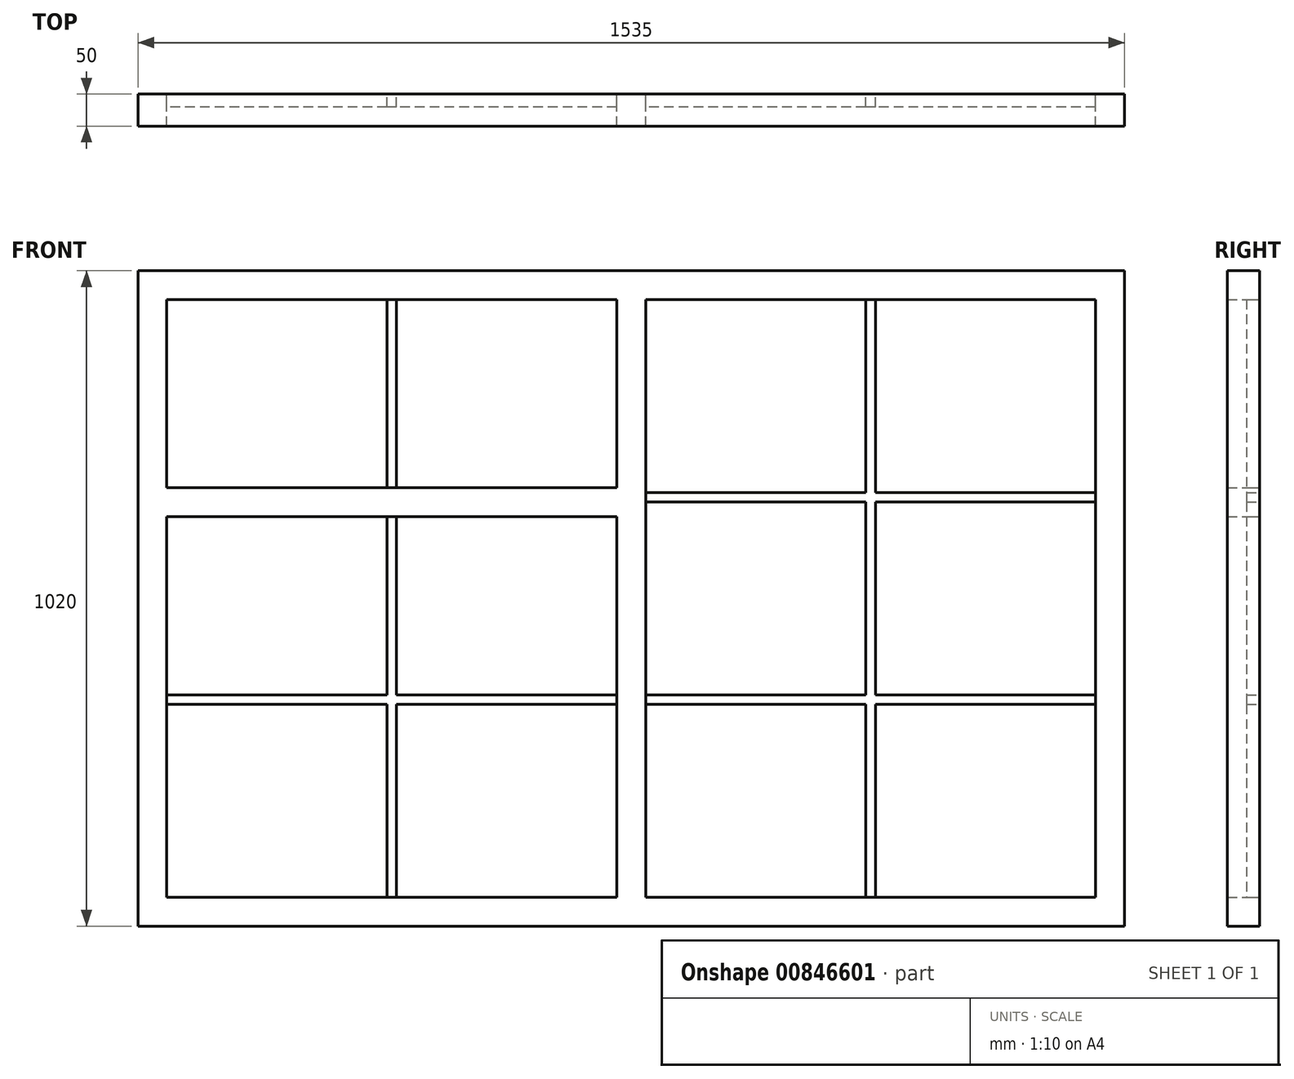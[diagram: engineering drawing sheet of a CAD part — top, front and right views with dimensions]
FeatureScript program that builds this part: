
annotation { "Feature Type Name" : "Feature", "Feature Type Description" : "" }
export const myFeature = defineFeature(function(context is Context, id is Id, definition is map)
    precondition{}
    {
        {
            var Q0;
            Q0=qCreatedBy(makeId("Front.planeOp"),FACE);
            var sketch = newSketch(context, id + "F0", { "sketchPlane" : qUnion([Q0])});
            skLineSegment(sketch, "E0.bottom", {"start": v(0, 0) * mm, "end": v(1535, 0) * mm});
            skLineSegment(sketch, "E0.top", {"start": v(0, 1020) * mm, "end": v(1535, 1020) * mm});
            skLineSegment(sketch, "E0.left", {"start": v(0, 0) * mm, "end": v(0, 1020) * mm});
            skLineSegment(sketch, "E0.right", {"start": v(1535, 0) * mm, "end": v(1535, 1020) * mm});
            skLineSegment(sketch, "E1.bottom", {"start": v(45, 975) * mm, "end": v(745, 975) * mm});
            skLineSegment(sketch, "E1.top", {"start": v(45, 45) * mm, "end": v(745, 45) * mm});
            skLineSegment(sketch, "E1.left", {"start": v(45, 975) * mm, "end": v(45, 45) * mm});
            skLineSegment(sketch, "E1.right", {"start": v(745, 975) * mm, "end": v(745, 45) * mm});
            skLineSegment(sketch, "E2.bottom", {"start": v(790, 975) * mm, "end": v(1490, 975) * mm});
            skLineSegment(sketch, "E2.top", {"start": v(790, 682.5) * mm, "end": v(1490, 682.5) * mm});
            skLineSegment(sketch, "E2.left", {"start": v(790, 975) * mm, "end": v(790, 682.5) * mm});
            skLineSegment(sketch, "E2.right", {"start": v(1490, 975) * mm, "end": v(1490, 682.5) * mm});
            skLineSegment(sketch, "E3.bottom", {"start": v(790, 637.5) * mm, "end": v(1490, 637.5) * mm});
            skLineSegment(sketch, "E3.top", {"start": v(790, 45) * mm, "end": v(1490, 45) * mm});
            skLineSegment(sketch, "E3.left", {"start": v(790, 637.5) * mm, "end": v(790, 45) * mm});
            skLineSegment(sketch, "E3.right", {"start": v(1490, 637.5) * mm, "end": v(1490, 45) * mm});
            skSolve(sketch);
        }
        {
            var Q0;
            Q0=qSketchRegion(id+"F0",true);
            extrude(context, id + "F1", {"entities" : qUnion([Q0]), "depth" : 50 * mm, "offsetDistance" : 25 * mm});
        }
        {
            var Q0;
            Q0=qCreatedBy(makeId("Front.planeOp"),FACE);
            var sketch = newSketch(context, id + "F2", { "sketchPlane" : qUnion([Q0])});
            skLineSegment(sketch, "E4.bottom", {"start": v(387.5, 975) * mm, "end": v(402.5, 975) * mm});
            skLineSegment(sketch, "E4.top", {"start": v(387.5, 45) * mm, "end": v(402.5, 45) * mm});
            skLineSegment(sketch, "E4.left", {"start": v(387.5, 975) * mm, "end": v(387.5, 675) * mm});
            skLineSegment(sketch, "E4.right", {"start": v(402.5, 975) * mm, "end": v(402.5, 675) * mm});
            skLineSegment(sketch, "E5.bottom", {"start": v(45, 675) * mm, "end": v(387.5, 675) * mm});
            skLineSegment(sketch, "E5.top", {"start": v(45, 660) * mm, "end": v(387.5, 660) * mm});
            skLineSegment(sketch, "E5.left", {"start": v(45, 675) * mm, "end": v(45, 660) * mm});
            skLineSegment(sketch, "E5.right", {"start": v(745, 675) * mm, "end": v(745, 660) * mm});
            skLineSegment(sketch, "E6.bottom", {"start": v(45, 360) * mm, "end": v(387.5, 360) * mm});
            skLineSegment(sketch, "E6.top", {"start": v(45, 345) * mm, "end": v(387.5, 345) * mm});
            skLineSegment(sketch, "E6.left", {"start": v(45, 360) * mm, "end": v(45, 345) * mm});
            skLineSegment(sketch, "E6.right", {"start": v(745, 360) * mm, "end": v(745, 345) * mm});
            skLineSegment(sketch, "E7.trimOffspring", {"start": v(402.5, 675) * mm, "end": v(745, 675) * mm});
            skLineSegment(sketch, "E8.trimOffspring", {"start": v(387.5, 660) * mm, "end": v(387.5, 360) * mm});
            skLineSegment(sketch, "E9.trimOffspring", {"start": v(402.5, 660) * mm, "end": v(745, 660) * mm});
            skLineSegment(sketch, "E10.trimOffspring", {"start": v(402.5, 660) * mm, "end": v(402.5, 360) * mm});
            skLineSegment(sketch, "E11.trimOffspring", {"start": v(402.5, 360) * mm, "end": v(745, 360) * mm});
            skLineSegment(sketch, "E12.trimOffspring", {"start": v(387.5, 345) * mm, "end": v(387.5, 45) * mm});
            skLineSegment(sketch, "E13.trimOffspring", {"start": v(402.5, 345) * mm, "end": v(745, 345) * mm});
            skLineSegment(sketch, "E14.trimOffspring", {"start": v(402.5, 345) * mm, "end": v(402.5, 45) * mm});
            skLineSegment(sketch, "E15.bottom", {"start": v(790, 360) * mm, "end": v(1132.5, 360) * mm});
            skLineSegment(sketch, "E15.top", {"start": v(790, 345) * mm, "end": v(1132.5, 345) * mm});
            skLineSegment(sketch, "E15.left", {"start": v(790, 360) * mm, "end": v(790, 345) * mm});
            skLineSegment(sketch, "E15.right", {"start": v(1490, 360) * mm, "end": v(1490, 345) * mm});
            skLineSegment(sketch, "E16.bottom", {"start": v(1132.5, 637.5) * mm, "end": v(1147.5, 637.5) * mm});
            skLineSegment(sketch, "E16.top", {"start": v(1132.5, 45) * mm, "end": v(1147.5, 45) * mm});
            skLineSegment(sketch, "E16.left", {"start": v(1132.5, 637.5) * mm, "end": v(1132.5, 360) * mm});
            skLineSegment(sketch, "E16.right", {"start": v(1147.5, 637.5) * mm, "end": v(1147.5, 360) * mm});
            skLineSegment(sketch, "E17.bottom", {"start": v(1132.5, 975) * mm, "end": v(1147.5, 975) * mm});
            skLineSegment(sketch, "E17.top", {"start": v(1132.5, 682.5) * mm, "end": v(1147.5, 682.5) * mm});
            skLineSegment(sketch, "E17.left", {"start": v(1132.5, 975) * mm, "end": v(1132.5, 682.5) * mm});
            skLineSegment(sketch, "E17.right", {"start": v(1147.5, 975) * mm, "end": v(1147.5, 682.5) * mm});
            skLineSegment(sketch, "E18.trimOffspring", {"start": v(1147.5, 360) * mm, "end": v(1490, 360) * mm});
            skLineSegment(sketch, "E19.trimOffspring", {"start": v(1132.5, 345) * mm, "end": v(1132.5, 45) * mm});
            skLineSegment(sketch, "E20.trimOffspring", {"start": v(1147.5, 345) * mm, "end": v(1490, 345) * mm});
            skLineSegment(sketch, "E21.trimOffspring", {"start": v(1147.5, 345) * mm, "end": v(1147.5, 45) * mm});
            skSolve(sketch);
        }
        {
            var Q0;
            Q0=qSketchRegion(id+"F2",true);
            extrude(context, id + "F3", {"entities" : qUnion([Q0]), "operationType" : NewBodyOperationType.ADD, "depth" : 20 * mm, "offsetDistance" : 25 * mm});
        }
        {
            var Q0;
            Q0=makeQuery(id+"F1.opExtrude","SWEPT_BODY",BODY,{"disambiguationData":[OSD([sQuery(id+"F0.wireOp",EDGE,"E0.bottom"),sQuery(id+"F0.wireOp",EDGE,"E0.top"),sQuery(id+"F0.wireOp",EDGE,"E0.left"),sQuery(id+"F0.wireOp",EDGE,"E0.right"),sQuery(id+"F0.wireOp",EDGE,"E1.bottom"),sQuery(id+"F0.wireOp",EDGE,"E1.top"),sQuery(id+"F0.wireOp",EDGE,"E1.left"),sQuery(id+"F0.wireOp",EDGE,"E1.right"),sQuery(id+"F0.wireOp",EDGE,"E2.bottom"),sQuery(id+"F0.wireOp",EDGE,"E2.top"),sQuery(id+"F0.wireOp",EDGE,"E2.left"),sQuery(id+"F0.wireOp",EDGE,"E2.right"),sQuery(id+"F0.wireOp",EDGE,"E3.bottom"),sQuery(id+"F0.wireOp",EDGE,"E3.top"),sQuery(id+"F0.wireOp",EDGE,"E3.left"),sQuery(id+"F0.wireOp",EDGE,"E3.right")])]});
            var Q1;
            Q1=makeQuery(id+"F1.opExtrude","SWEPT_FACE",FACE,{"disambiguationData":[OSD([sQuery(id+"F0.wireOp",EDGE,"E0.right")])]});
            mirror(context, id + "F4", {"entities" : qUnion([Q0]), "mirrorPlane" : qUnion([Q1])});
        }
        {
            var Q0;
            Q0=makeQuery(id+"F1.opExtrude","SWEPT_BODY",BODY,{"disambiguationData":[OSD([sQuery(id+"F0.wireOp",EDGE,"E0.bottom"),sQuery(id+"F0.wireOp",EDGE,"E0.top"),sQuery(id+"F0.wireOp",EDGE,"E0.left"),sQuery(id+"F0.wireOp",EDGE,"E0.right"),sQuery(id+"F0.wireOp",EDGE,"E1.bottom"),sQuery(id+"F0.wireOp",EDGE,"E1.top"),sQuery(id+"F0.wireOp",EDGE,"E1.left"),sQuery(id+"F0.wireOp",EDGE,"E1.right"),sQuery(id+"F0.wireOp",EDGE,"E2.bottom"),sQuery(id+"F0.wireOp",EDGE,"E2.top"),sQuery(id+"F0.wireOp",EDGE,"E2.left"),sQuery(id+"F0.wireOp",EDGE,"E2.right"),sQuery(id+"F0.wireOp",EDGE,"E3.bottom"),sQuery(id+"F0.wireOp",EDGE,"E3.top"),sQuery(id+"F0.wireOp",EDGE,"E3.left"),sQuery(id+"F0.wireOp",EDGE,"E3.right")])]});
            deleteBodies(context, id + "F5", {"entities" : qUnion([Q0])});
        }
    });
